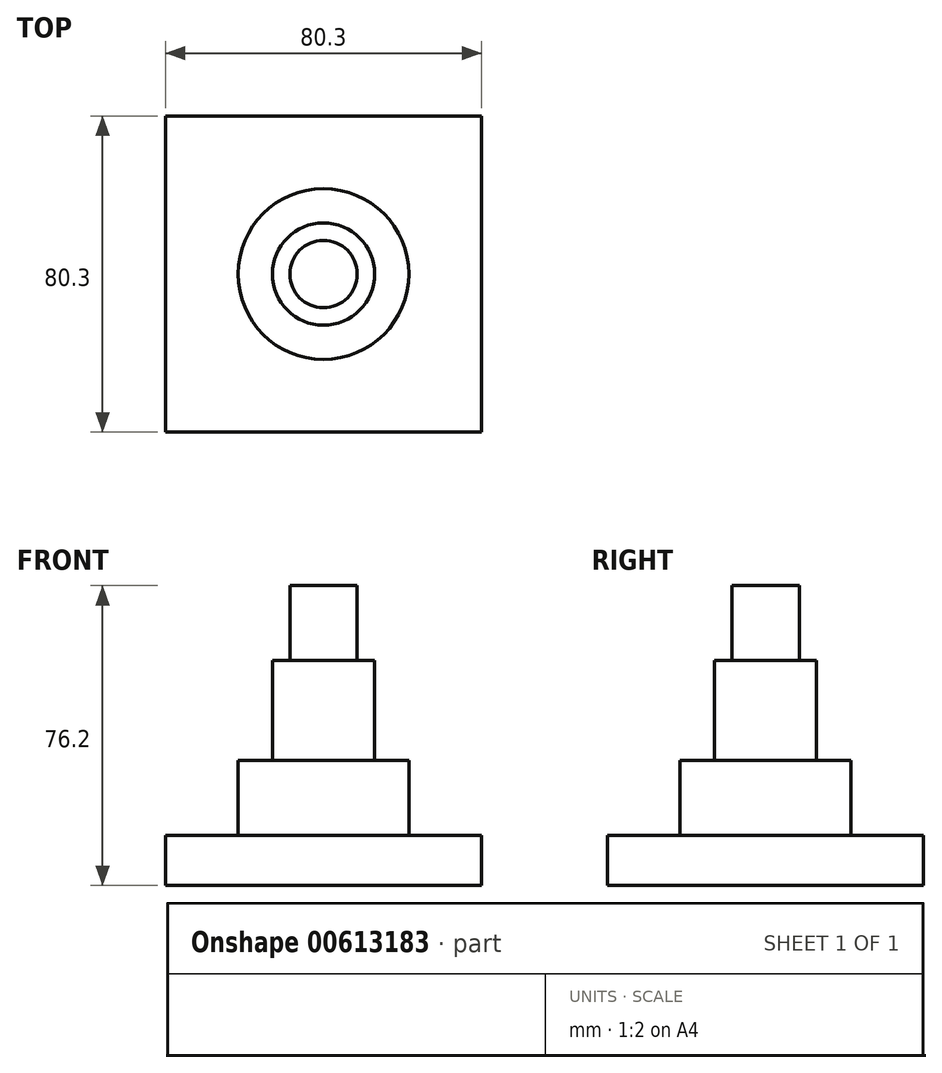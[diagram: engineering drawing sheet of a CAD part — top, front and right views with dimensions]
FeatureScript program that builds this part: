
annotation { "Feature Type Name" : "Feature", "Feature Type Description" : "" }
export const myFeature = defineFeature(function(context is Context, id is Id, definition is map)
    precondition{}
    {
        {
            var Q0;
            Q0=qCreatedBy(makeId("Top.planeOp"),FACE);
            var sketch = newSketch(context, id + "F0", { "sketchPlane" : qUnion([Q0])});
            skCircle(sketch, "E0.cCircle", {"center": v(0, 0) * mm, "radius": 40.15 * mm, "construction": true});
            skLineSegment(sketch, "E0.0", {"start": v(40.15, 40.15) * mm, "end": v(40.15, -40.15) * mm});
            skLineSegment(sketch, "E0.1", {"start": v(40.15, -40.15) * mm, "end": v(-40.15, -40.15) * mm});
            skLineSegment(sketch, "E0.2", {"start": v(-40.15, -40.15) * mm, "end": v(-40.15, 40.15) * mm});
            skLineSegment(sketch, "E0.3", {"start": v(-40.15, 40.15) * mm, "end": v(40.15, 40.15) * mm});
            skPoint(sketch, "E0.0.midPoint", {"position": v(40.15, 0) * mm});
            skSolve(sketch);
        }
        {
            var Q0;
            Q0 = qSketchRegion(id + "F0", true);
            extrude(context, id + "F1", {"entities" : qUnion([Q0]), "depth" : 12.7 * mm, "offsetDistance" : 25.4 * mm});
        }
        {
            var Q0;
            Q0=makeQuery(id+"F1.opExtrude","CAP_FACE",FACE,{"disambiguationData":[OSD([sQuery(id+"F0.wireOp",EDGE,"E0.0"),sQuery(id+"F0.wireOp",EDGE,"E0.1"),sQuery(id+"F0.wireOp",EDGE,"E0.2"),sQuery(id+"F0.wireOp",EDGE,"E0.3")])],"isStart":false});
            var sketch = newSketch(context, id + "F2", { "sketchPlane" : qUnion([Q0])});
            skCircle(sketch, "E1", {"center": v(0, 0) * mm, "radius": 21.69 * mm});
            skSolve(sketch);
        }
        {
            var Q0;
            Q0 = qSketchRegion(id + "F2", true);
            extrude(context, id + "F3", {"entities" : qUnion([Q0]), "operationType" : NewBodyOperationType.ADD, "depth" : 19.05 * mm, "offsetDistance" : 25.4 * mm});
        }
        {
            var Q0;
            Q0=makeQuery(id+"F3.opExtrude","CAP_FACE",FACE,{"disambiguationData":[OSD([sQuery(id+"F2.wireOp",EDGE,"E1")])],"isStart":false});
            var sketch = newSketch(context, id + "F4", { "sketchPlane" : qUnion([Q0])});
            skCircle(sketch, "E2", {"center": v(0, 0) * mm, "radius": 12.98 * mm});
            skSolve(sketch);
        }
        {
            var Q0;
            Q0 = qSketchRegion(id + "F4", true);
            extrude(context, id + "F5", {"entities" : qUnion([Q0]), "operationType" : NewBodyOperationType.ADD, "depth" : 25.4 * mm, "offsetDistance" : 25.4 * mm});
        }
        {
            var Q0;
            Q0=makeQuery(id+"F5.opExtrude","CAP_FACE",FACE,{"disambiguationData":[OSD([sQuery(id+"F4.wireOp",EDGE,"E2")])],"isStart":false});
            var sketch = newSketch(context, id + "F6", { "sketchPlane" : qUnion([Q0])});
            skCircle(sketch, "E3", {"center": v(0, 0) * mm, "radius": 8.56 * mm});
            skSolve(sketch);
        }
        {
            var Q0;
            Q0 = qSketchRegion(id + "F6", true);
            extrude(context, id + "F7", {"entities" : qUnion([Q0]), "operationType" : NewBodyOperationType.ADD, "depth" : 19.05 * mm, "offsetDistance" : 25.4 * mm});
        }
    });
